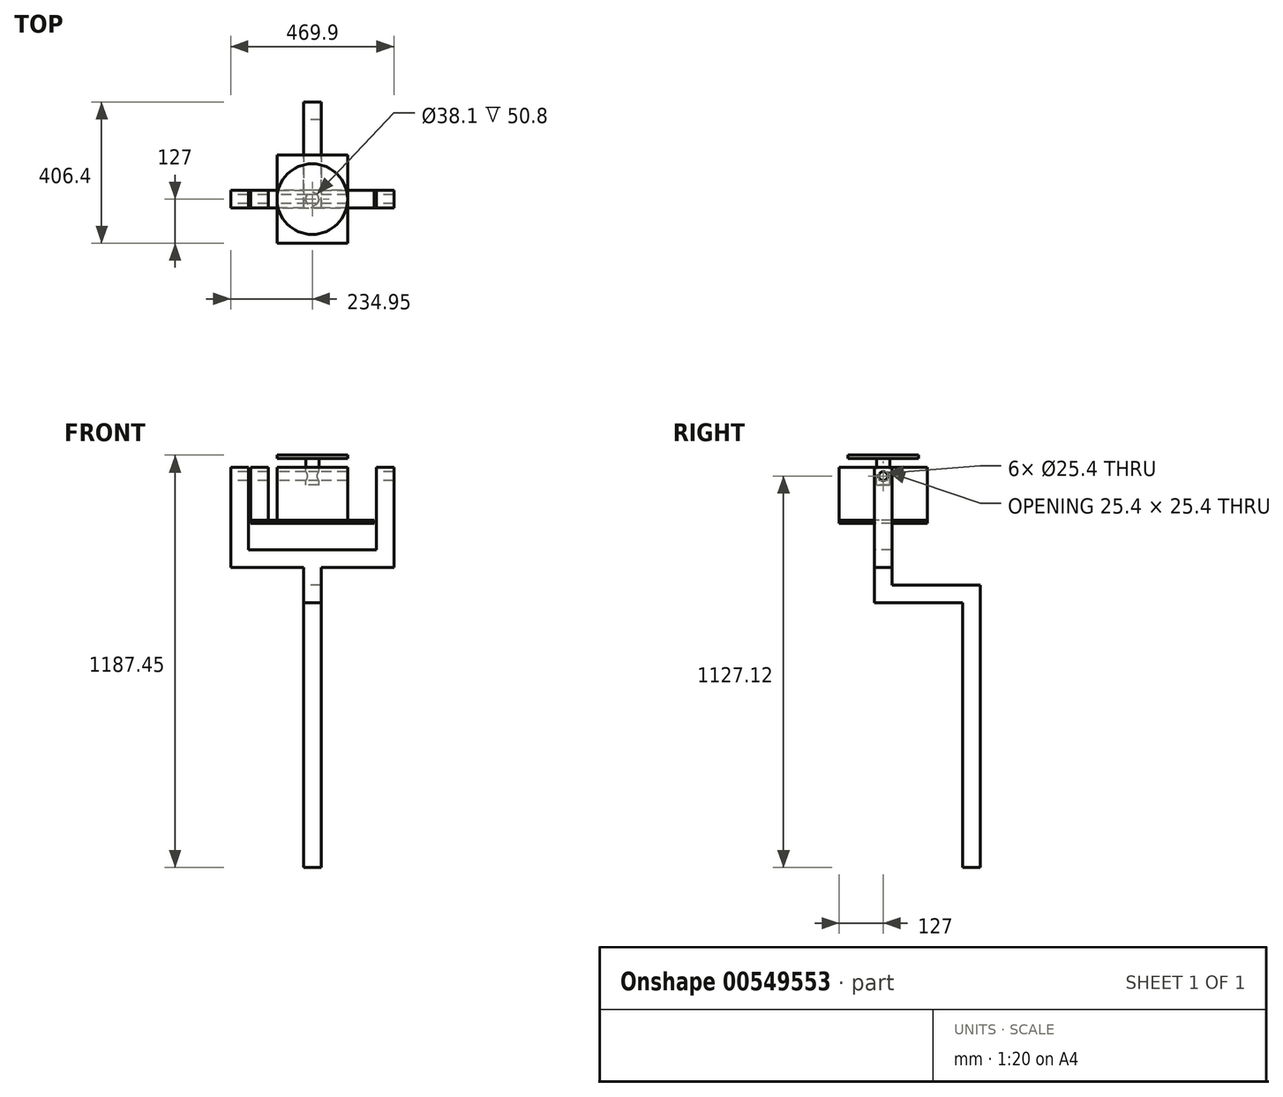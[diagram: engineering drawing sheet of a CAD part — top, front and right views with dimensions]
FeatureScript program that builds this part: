
annotation { "Feature Type Name" : "Feature", "Feature Type Description" : "" }
export const myFeature = defineFeature(function(context is Context, id is Id, definition is map)
    precondition{}
    {
        {
            var Q0;
            Q0=qCreatedBy(makeId("Top.planeOp"),FACE);
            var sketch = newSketch(context, id + "F0", { "sketchPlane" : qUnion([Q0])});
            skLineSegment(sketch, "E0.bottom", {"start": v(-101.6, 127) * mm, "end": v(101.6, 127) * mm});
            skLineSegment(sketch, "E0.top", {"start": v(-101.6, -127) * mm, "end": v(101.6, -127) * mm});
            skLineSegment(sketch, "E0.left", {"start": v(-101.6, 127) * mm, "end": v(-101.6, -127) * mm});
            skLineSegment(sketch, "E0.right", {"start": v(101.6, 127) * mm, "end": v(101.6, -127) * mm});
            skSolve(sketch);
        }
        {
            var Q0;
            Q0 = qSketchRegion(id + "F0", true);
            extrude(context, id + "F1", {"entities" : qUnion([Q0]), "depth" : 152.4 * mm, "offsetDistance" : 25.4 * mm});
        }
        {
            var Q0;
            Q0=makeQuery(id+"F1.opExtrude","CAP_FACE",FACE,{"disambiguationData":[OSD([sQuery(id+"F0.wireOp",EDGE,"E0.bottom"),sQuery(id+"F0.wireOp",EDGE,"E0.top"),sQuery(id+"F0.wireOp",EDGE,"E0.left"),sQuery(id+"F0.wireOp",EDGE,"E0.right")])],"isStart":false});
            var sketch = newSketch(context, id + "F2", { "sketchPlane" : qUnion([Q0])});
            skCircle(sketch, "E1", {"center": v(0, 0) * mm, "radius": 19.05 * mm});
            skSolve(sketch);
        }
        {
            var Q0;
            Q0 = qSketchRegion(id + "F2", true);
            extrude(context, id + "F3", {"entities" : qUnion([Q0]), "operationType" : NewBodyOperationType.REMOVE, "oppositeDirection" : true, "depth" : 50.8 * mm, "offsetDistance" : 25.4 * mm});
        }
        {
            var Q0;
            Q0=qCreatedBy(makeId("Front.planeOp"),FACE);
            var sketch = newSketch(context, id + "F4", { "sketchPlane" : qUnion([Q0])});
            skLineSegment(sketch, "E2", {"start": v(0, 187.33) * mm, "end": v(0, 101.6) * mm});
            skLineSegment(sketch, "E3", {"start": v(0, 101.6) * mm, "end": v(19.05, 101.6) * mm});
            skLineSegment(sketch, "E4", {"start": v(19.05, 101.6) * mm, "end": v(19.05, 177.8) * mm});
            skLineSegment(sketch, "E5", {"start": v(19.05, 177.8) * mm, "end": v(101.6, 177.8) * mm});
            skLineSegment(sketch, "E6", {"start": v(101.6, 177.8) * mm, "end": v(101.6, 187.33) * mm});
            skLineSegment(sketch, "E7", {"start": v(101.6, 187.33) * mm, "end": v(0, 187.33) * mm});
            skSolve(sketch);
        }
        {
            var Q0;
            Q0 = qSketchRegion(id + "F4", true);
            var Q1;
            Q1=sQuery(id+"F4.wireOp",EDGE,"E2");
            revolve(context, id + "F5", {"entities" : qUnion([Q0]), "axis" : qUnion([Q1]), "revolveType" : RevolveType.FULL});
        }
        {
            var Q0;
            Q0=makeQuery(id+"F1.opExtrude","CAP_FACE",FACE,{"disambiguationData":[OSD([sQuery(id+"F0.wireOp",EDGE,"E0.bottom"),sQuery(id+"F0.wireOp",EDGE,"E0.top"),sQuery(id+"F0.wireOp",EDGE,"E0.left"),sQuery(id+"F0.wireOp",EDGE,"E0.right")])],"isStart":true});
            var sketch = newSketch(context, id + "F6", { "sketchPlane" : qUnion([Q0])});
            skLineSegment(sketch, "E8.bottom", {"start": v(-101.6, 127) * mm, "end": v(101.6, 127) * mm});
            skLineSegment(sketch, "E8.top", {"start": v(-101.6, -127) * mm, "end": v(101.6, -127) * mm});
            skLineSegment(sketch, "E8.left", {"start": v(-101.6, 127) * mm, "end": v(-101.6, 25.4) * mm});
            skLineSegment(sketch, "E8.right", {"start": v(101.6, 127) * mm, "end": v(101.6, 25.4) * mm});
            skLineSegment(sketch, "E9", {"start": v(101.6, 25.4) * mm, "end": v(177.8, 25.4) * mm});
            skLineSegment(sketch, "E10", {"start": v(177.8, 25.4) * mm, "end": v(177.8, -25.4) * mm});
            skLineSegment(sketch, "E11", {"start": v(177.8, -25.4) * mm, "end": v(101.6, -25.4) * mm});
            skLineSegment(sketch, "E12", {"start": v(-177.8, -25.4) * mm, "end": v(-177.8, 25.4) * mm});
            skLineSegment(sketch, "E13", {"start": v(-177.8, 25.4) * mm, "end": v(-101.6, 25.4) * mm});
            skLineSegment(sketch, "E14.trimOffspring", {"start": v(-101.6, -25.4) * mm, "end": v(-101.6, -127) * mm});
            skLineSegment(sketch, "E15.trimOffspring", {"start": v(101.6, -25.4) * mm, "end": v(101.6, -127) * mm});
            skLineSegment(sketch, "E16.trimOffspring", {"start": v(-101.6, -25.4) * mm, "end": v(-177.8, -25.4) * mm});
            skSolve(sketch);
        }
        {
            var Q0;
            Q0 = qSketchRegion(id + "F6", true);
            extrude(context, id + "F7", {"entities" : qUnion([Q0]), "depth" : 9.52 * mm, "offsetDistance" : 25.4 * mm});
        }
        {
            var Q0;
            Q0=makeQuery(id+"F7.opExtrude","CAP_FACE",FACE,{"disambiguationData":[OSD([sQuery(id+"F6.wireOp",EDGE,"E8.bottom"),sQuery(id+"F6.wireOp",EDGE,"E8.top"),sQuery(id+"F6.wireOp",EDGE,"E8.left"),sQuery(id+"F6.wireOp",EDGE,"E8.right"),sQuery(id+"F6.wireOp",EDGE,"E9"),sQuery(id+"F6.wireOp",EDGE,"E10"),sQuery(id+"F6.wireOp",EDGE,"E11"),sQuery(id+"F6.wireOp",EDGE,"E12"),sQuery(id+"F6.wireOp",EDGE,"E13"),sQuery(id+"F6.wireOp",EDGE,"E14.trimOffspring"),sQuery(id+"F6.wireOp",EDGE,"E15.trimOffspring"),sQuery(id+"F6.wireOp",EDGE,"E16.trimOffspring")])],"isStart":true});
            var sketch = newSketch(context, id + "F8", { "sketchPlane" : qUnion([Q0])});
            skLineSegment(sketch, "E17.bottom", {"start": v(-177.8, 25.4) * mm, "end": v(-127, 25.4) * mm});
            skLineSegment(sketch, "E17.top", {"start": v(-177.8, -25.4) * mm, "end": v(-127, -25.4) * mm});
            skLineSegment(sketch, "E17.left", {"start": v(-177.8, 25.4) * mm, "end": v(-177.8, -25.4) * mm});
            skLineSegment(sketch, "E17.right", {"start": v(-127, 25.4) * mm, "end": v(-127, -25.4) * mm});
            skSolve(sketch);
        }
        {
            var Q0;
            Q0 = qSketchRegion(id + "F8", true);
            var Q1;
            Q1=makeQuery(id+"F1.opExtrude","CAP_FACE",FACE,{"disambiguationData":[OSD([sQuery(id+"F0.wireOp",EDGE,"E0.bottom"),sQuery(id+"F0.wireOp",EDGE,"E0.top"),sQuery(id+"F0.wireOp",EDGE,"E0.left"),sQuery(id+"F0.wireOp",EDGE,"E0.right")])],"isStart":false});
            extrude(context, id + "F9", {"entities" : qUnion([Q0]), "endBound" : BoundingType.UP_TO_SURFACE, "depth" : 25.4 * mm, "endBoundEntityFace" : qUnion([Q1]), "offsetDistance" : 25.4 * mm});
        }
        {
            var Q0;
            Q0=makeQuery(id+"F9.opExtrude","SWEPT_FACE",FACE,{"disambiguationData":[OSD([sQuery(id+"F8.wireOp",EDGE,"E17.left")])]});
            var sketch = newSketch(context, id + "F10", { "sketchPlane" : qUnion([Q0])});
            skCircle(sketch, "E18", {"center": v(0, 127) * mm, "radius": 12.7 * mm});
            skSolve(sketch);
        }
        {
            var Q0;
            Q0 = qSketchRegion(id + "F10", true);
            extrude(context, id + "F11", {"entities" : qUnion([Q0]), "operationType" : NewBodyOperationType.REMOVE, "endBound" : BoundingType.UP_TO_NEXT, "oppositeDirection" : true, "depth" : 25.4 * mm, "offsetDistance" : 25.4 * mm});
        }
        {
            var Q0;
            Q0=makeQuery(id+"F9.opExtrude","SWEPT_FACE",FACE,{"disambiguationData":[OSD([sQuery(id+"F8.wireOp",EDGE,"E17.right")])]});
            var sketch = newSketch(context, id + "F12", { "sketchPlane" : qUnion([Q0])});
            skCircle(sketch, "E19", {"center": v(0, 127) * mm, "radius": 12.7 * mm});
            skSolve(sketch);
        }
        {
            var Q0;
            Q0 = qSketchRegion(id + "F12", true);
            extrude(context, id + "F13", {"entities" : qUnion([Q0]), "oppositeDirection" : true, "depth" : 107.95 * mm, "offsetDistance" : 25.4 * mm});
        }
        {
            var Q0;
            Q0=makeQuery(id+"F9.opExtrude","SWEPT_FACE",FACE,{"disambiguationData":[OSD([sQuery(id+"F8.wireOp",EDGE,"E17.top")])]});
            var sketch = newSketch(context, id + "F14", { "sketchPlane" : qUnion([Q0])});
            skLineSegment(sketch, "E20", {"start": v(-184.15, 152.4) * mm, "end": v(-184.15, -85.73) * mm});
            skLineSegment(sketch, "E21", {"start": v(-184.15, -85.73) * mm, "end": v(184.15, -85.72) * mm});
            skLineSegment(sketch, "E22", {"start": v(184.15, -85.72) * mm, "end": v(184.15, 152.4) * mm});
            skLineSegment(sketch, "E23", {"start": v(184.15, 152.4) * mm, "end": v(234.95, 152.4) * mm});
            skLineSegment(sketch, "E24", {"start": v(234.95, 152.4) * mm, "end": v(234.95, -136.52) * mm});
            skLineSegment(sketch, "E25", {"start": v(234.95, -136.52) * mm, "end": v(-234.95, -136.53) * mm});
            skLineSegment(sketch, "E26", {"start": v(-234.95, -136.53) * mm, "end": v(-234.95, 152.4) * mm});
            skLineSegment(sketch, "E27", {"start": v(-234.95, 152.4) * mm, "end": v(-184.15, 152.4) * mm});
            skSolve(sketch);
        }
        {
            var Q0;
            Q0 = qSketchRegion(id + "F14", true);
            var Q1;
            Q1=makeQuery(id+"F9.opExtrude","SWEPT_FACE",FACE,{"disambiguationData":[OSD([sQuery(id+"F8.wireOp",EDGE,"E17.bottom")])]});
            extrude(context, id + "F15", {"entities" : qUnion([Q0]), "endBound" : BoundingType.UP_TO_SURFACE, "oppositeDirection" : true, "depth" : 25.4 * mm, "endBoundEntityFace" : qUnion([Q1]), "offsetDistance" : 25.4 * mm});
        }
        {
            var Q0;
            Q0=makeQuery(id+"F15.opExtrude","SWEPT_FACE",FACE,{"disambiguationData":[OSD([sQuery(id+"F14.wireOp",EDGE,"E26")])]});
            var sketch = newSketch(context, id + "F16", { "sketchPlane" : qUnion([Q0])});
            skCircle(sketch, "E28", {"center": v(0, 127) * mm, "radius": 12.7 * mm});
            skSolve(sketch);
        }
        {
            var Q0;
            Q0 = qSketchRegion(id + "F16", true);
            var Q1;
            Q1=makeQuery(id+"F15.opExtrude","SWEPT_FACE",FACE,{"disambiguationData":[OSD([sQuery(id+"F14.wireOp",EDGE,"E24")])]});
            extrude(context, id + "F17", {"entities" : qUnion([Q0]), "operationType" : NewBodyOperationType.REMOVE, "endBound" : BoundingType.UP_TO_SURFACE, "oppositeDirection" : true, "depth" : 25.4 * mm, "endBoundEntityFace" : qUnion([Q1]), "offsetDistance" : 25.4 * mm});
        }
        {
            var Q0;
            Q0=qCreatedBy(makeId("Right.planeOp"),FACE);
            var sketch = newSketch(context, id + "F18", { "sketchPlane" : qUnion([Q0])});
            skLineSegment(sketch, "E29", {"start": v(25.4, -136.53) * mm, "end": v(25.4, -187.32) * mm});
            skLineSegment(sketch, "E30", {"start": v(25.4, -187.32) * mm, "end": v(279.4, -187.32) * mm});
            skLineSegment(sketch, "E31", {"start": v(279.4, -187.32) * mm, "end": v(279.4, -1000.13) * mm});
            skLineSegment(sketch, "E32", {"start": v(279.4, -1000.13) * mm, "end": v(228.6, -1000.13) * mm});
            skLineSegment(sketch, "E33", {"start": v(228.6, -1000.13) * mm, "end": v(228.6, -238.12) * mm});
            skLineSegment(sketch, "E34", {"start": v(228.6, -238.12) * mm, "end": v(-25.4, -238.13) * mm});
            skLineSegment(sketch, "E35", {"start": v(-25.4, -238.13) * mm, "end": v(-25.4, -136.53) * mm});
            skLineSegment(sketch, "E36", {"start": v(-25.4, -136.53) * mm, "end": v(25.4, -136.53) * mm});
            skSolve(sketch);
        }
        {
            var Q0;
            Q0 = qSketchRegion(id + "F18", true);
            extrude(context, id + "F19", {"entities" : qUnion([Q0]), "operationType" : NewBodyOperationType.ADD, "endBound" : BoundingType.SYMMETRIC, "depth" : 50.8 * mm, "offsetDistance" : 25.4 * mm});
        }
    });
